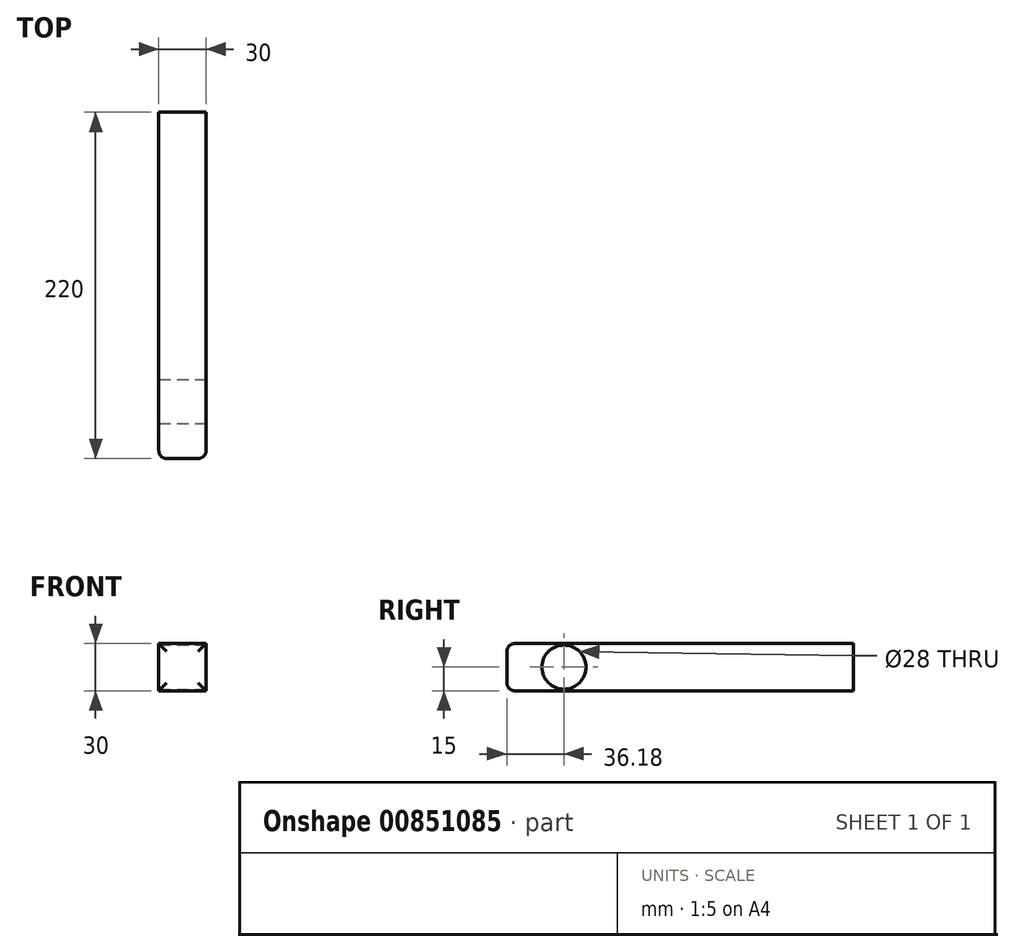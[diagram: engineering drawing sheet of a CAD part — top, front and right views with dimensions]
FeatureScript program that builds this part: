
annotation { "Feature Type Name" : "Feature", "Feature Type Description" : "" }
export const myFeature = defineFeature(function(context is Context, id is Id, definition is map)
    precondition{}
    {
        {
            var Q0;
            Q0=qCreatedBy(makeId("Front.planeOp"),FACE);
            var sketch = newSketch(context, id + "F0", { "sketchPlane" : qUnion([Q0])});
            skLineSegment(sketch, "E0.bottom", {"start": v(-15, 15) * mm, "end": v(15, 15) * mm});
            skLineSegment(sketch, "E0.top", {"start": v(-15, -15) * mm, "end": v(15, -15) * mm});
            skLineSegment(sketch, "E0.left", {"start": v(-15, 15) * mm, "end": v(-15, -15) * mm});
            skLineSegment(sketch, "E0.right", {"start": v(15, 15) * mm, "end": v(15, -15) * mm});
            skSolve(sketch);
        }
        {
            var Q0;
            Q0=makeQuery(id+"F0.imprint","IMPRINT",FACE,{"disambiguationData":[TD([[makeQuery(id+"F0.imprint","IMPRINT",EDGE,{"derivedFrom":sQuery(id+"F0.wireOp",EDGE,"E0.bottom")}),-1.0]])]});
            extrude(context, id + "F1", {"entities" : qUnion([Q0]), "depth" : 220 * mm, "offsetDistance" : 25 * mm});
        }
        {
            var Q0;
            Q0=makeQuery(id+"F1.opExtrude","CAP_EDGE",EDGE,{"disambiguationData":[OSD([sQuery(id+"F0.wireOp",EDGE,"E0.right")])],"isStart":false});
            var Q1;
            Q1=makeQuery(id+"F1.opExtrude","CAP_EDGE",EDGE,{"disambiguationData":[OSD([sQuery(id+"F0.wireOp",EDGE,"E0.left")])],"isStart":false});
            var Q2;
            Q2=makeQuery(id+"F1.opExtrude","CAP_EDGE",EDGE,{"disambiguationData":[OSD([sQuery(id+"F0.wireOp",EDGE,"E0.bottom")])],"isStart":false});
            var Q3;
            Q3=makeQuery(id+"F1.opExtrude","CAP_EDGE",EDGE,{"disambiguationData":[OSD([sQuery(id+"F0.wireOp",EDGE,"E0.top")])],"isStart":false});
            fillet(context, id + "F2", {"entities" : qUnion([Q0, Q1, Q2, Q3]), "radius" : 5 * mm, "tangentPropagation" : true, "allowEdgeOverflow" : false});
        }
        {
            var Q0;
            Q0=makeQuery(id+"F1.opExtrude","SWEPT_FACE",FACE,{"disambiguationData":[OSD([sQuery(id+"F0.wireOp",EDGE,"E0.right")])]});
            var sketch = newSketch(context, id + "F3", { "sketchPlane" : qUnion([Q0])});
            skCircle(sketch, "E1", {"center": v(-600, 0) * mm, "radius": 15 * mm});
            skCircle(sketch, "E2", {"center": v(-183.82, 0) * mm, "radius": 14 * mm});
            skSolve(sketch);
        }
        {
            var Q0;
            {var subQ0=sQuery(id+"F3.wireOp",EDGE,"E2");var subQ1=sQuery(id+"F0.wireOp",EDGE,"E0.right");var subQ2=makeQuery(id+"F3.imprint","INTERSECT",VERTEX,{"derivedFrom":[makeQuery(id+"F1.opExtrude","SWEPT_EDGE",EDGE,{"disambiguationData":[OSD([sQuery(id+"F0.wireOp",EDGE,"E0.bottom"),subQ1])]}),subQ0]});Q0=makeQuery(id+"F3.imprint","IMPRINT",FACE,{"disambiguationData":[TD([[makeQuery(id+"F3.imprint","IMPRINT",EDGE,{"disambiguationData":[TD([[subQ2,-1.0]])],"derivedFrom":subQ0}),1.0]])]});}
            extrude(context, id + "F4", {"entities" : qUnion([Q0]), "operationType" : NewBodyOperationType.REMOVE, "oppositeDirection" : true, "depth" : 40 * mm, "offsetDistance" : 25 * mm});
        }
    });
